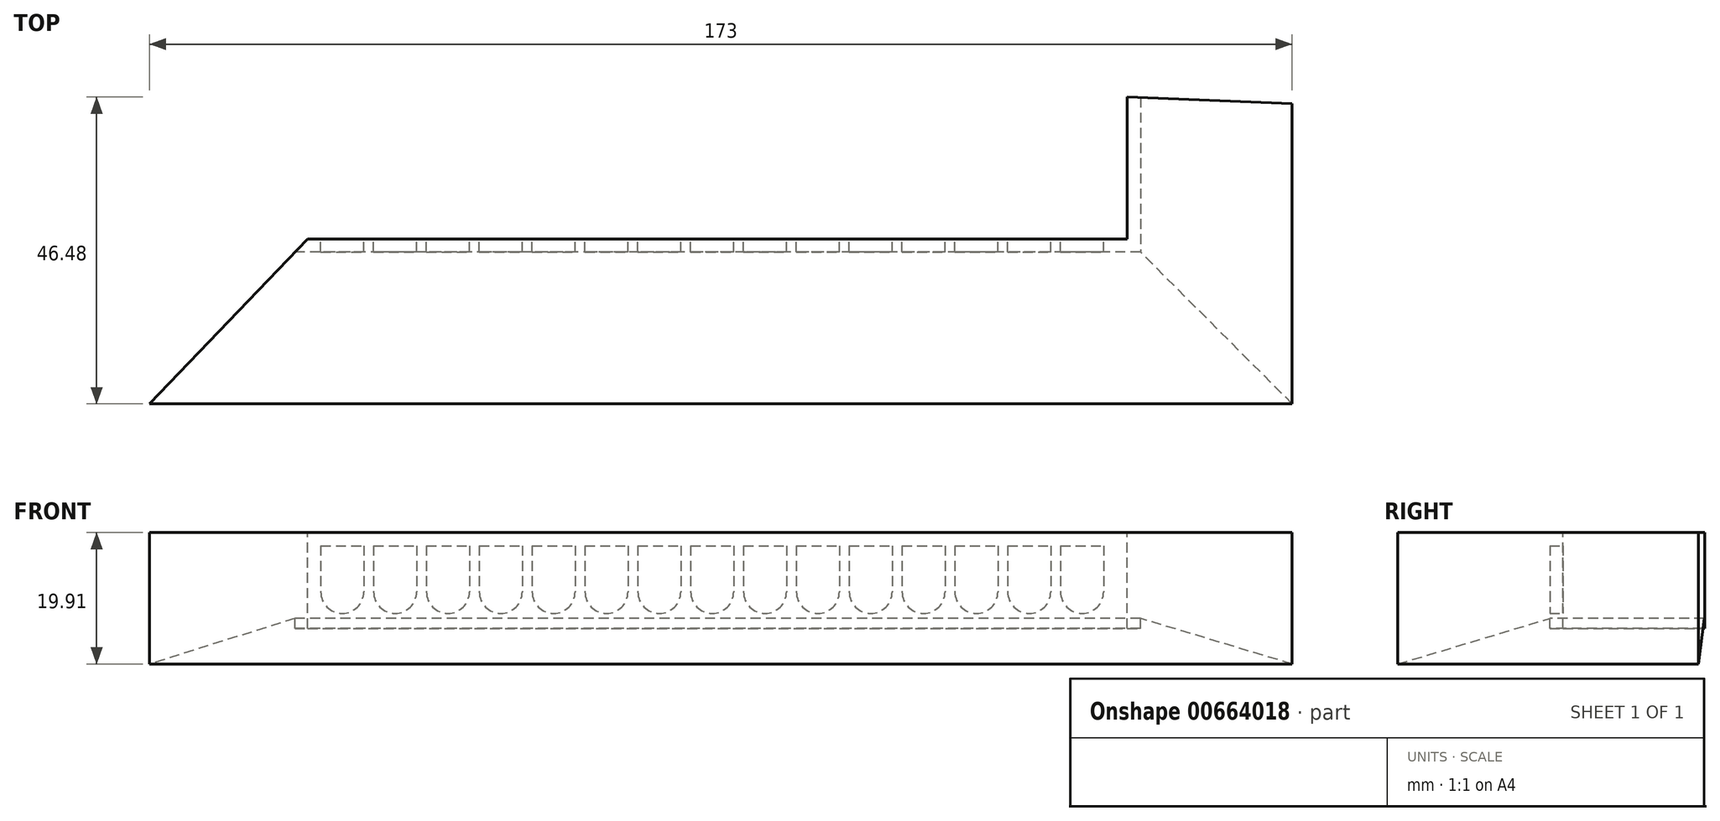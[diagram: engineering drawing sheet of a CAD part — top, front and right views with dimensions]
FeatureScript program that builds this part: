
annotation { "Feature Type Name" : "Feature", "Feature Type Description" : "" }
export const myFeature = defineFeature(function(context is Context, id is Id, definition is map)
    precondition{}
    {
        {
            var Q0;
            Q0=qCreatedBy(makeId("Top.planeOp"),FACE);
            var sketch = newSketch(context, id + "F0", { "sketchPlane" : qUnion([Q0])});
            skLineSegment(sketch, "E0", {"start": v(0, 0) * mm, "end": v(0, 45.5) * mm});
            skLineSegment(sketch, "E1", {"start": v(0, 45.5) * mm, "end": v(-22.98, 46.4) * mm});
            skLineSegment(sketch, "E2", {"start": v(-22.98, 46.4) * mm, "end": v(-22.98, 23) * mm});
            skLineSegment(sketch, "E3", {"start": v(-22.98, 23) * mm, "end": v(-150.98, 23) * mm});
            skLineSegment(sketch, "E4", {"start": v(-43.34, 0) * mm, "end": v(0, 0) * mm});
            skLineSegment(sketch, "E5", {"start": v(-150.98, 23) * mm, "end": v(-173, 0) * mm});
            skLineSegment(sketch, "E6", {"start": v(-173, 0) * mm, "end": v(-43.34, 0) * mm});
            skSolve(sketch);
        }
        {
            var Q0;
            Q0=makeQuery(id+"F0.imprint","IMPRINT",FACE,{"disambiguationData":[TD([[makeQuery(id+"F0.imprint","IMPRINT",EDGE,{"derivedFrom":sQuery(id+"F0.wireOp",EDGE,"E0")}),1.0]])]});
            extrude(context, id + "F1", {"entities" : qUnion([Q0]), "oppositeDirection" : true, "depth" : 13 * mm, "offsetDistance" : 25 * mm});
        }
        {
            var Q0;
            Q0=makeQuery(id+"F1.opExtrude","SWEPT_FACE",FACE,{"disambiguationData":[OSD([sQuery(id+"F0.wireOp",EDGE,"E4"),sQuery(id+"F0.wireOp",EDGE,"E6")])]});
            var sketch = newSketch(context, id + "F2", { "sketchPlane" : qUnion([Q0])});
            skLineSegment(sketch, "E7.0.0", {"start": v(-22.98, 0) * mm, "end": v(0, 0) * mm});
            skLineSegment(sketch, "E7.0.1", {"start": v(0, 0) * mm, "end": v(0, -13) * mm});
            skLineSegment(sketch, "E7.0.2", {"start": v(0, -13) * mm, "end": v(-22.98, -13) * mm});
            skLineSegment(sketch, "E7.0.3", {"start": v(-22.98, -13) * mm, "end": v(-22.98, 0) * mm});
            skLineSegment(sketch, "E8", {"start": v(-22.98, -13) * mm, "end": v(-20.98, -13) * mm});
            skLineSegment(sketch, "E9", {"start": v(-20.98, -13) * mm, "end": v(-22.98, -13) * mm});
            skLineSegment(sketch, "E10", {"start": v(-22.98, -13) * mm, "end": v(0, -19.91) * mm});
            skLineSegment(sketch, "E11", {"start": v(0, -19.91) * mm, "end": v(0, -13) * mm});
            skSolve(sketch);
        }
        {
            var Q0;
            {var subQ0=sQuery(id+"F2.wireOp",EDGE,"E10");Q0=makeQuery(id+"F2.imprint","IMPRINT",FACE,{"disambiguationData":[TD([[makeQuery(id+"F2.imprint","IMPRINT",EDGE,{"derivedFrom":subQ0}),1.0]])]});}
            var Q1;
            Q1=makeQuery(id+"F1.opExtrude","SWEPT_FACE",FACE,{"disambiguationData":[OSD([sQuery(id+"F0.wireOp",EDGE,"E1")])]});
            extrude(context, id + "F3", {"entities" : qUnion([Q0]), "operationType" : NewBodyOperationType.ADD, "endBound" : BoundingType.UP_TO_SURFACE, "oppositeDirection" : true, "depth" : 25 * mm, "endBoundEntityFace" : qUnion([Q1]), "offsetDistance" : 25 * mm});
        }
        {
            var Q0;
            Q0=makeQuery(id+"F3.boolean.opBoolean","MERGE",FACE,{"derivedFrom":[makeQuery(id+"F1.opExtrude","SWEPT_FACE",FACE,{"disambiguationData":[OSD([sQuery(id+"F0.wireOp",EDGE,"E0")])]}),makeQuery(id+"F3.opExtrude","SWEPT_FACE",FACE,{"disambiguationData":[OSD([sQuery(id+"F2.wireOp",EDGE,"E11")])]})]});
            var sketch = newSketch(context, id + "F4", { "sketchPlane" : qUnion([Q0])});
            skLineSegment(sketch, "E12.0.0", {"start": v(0, 0) * mm, "end": v(23, 0) * mm});
            skLineSegment(sketch, "E12.0.1", {"start": v(23, 0) * mm, "end": v(23, -13) * mm});
            skLineSegment(sketch, "E12.0.2", {"start": v(23, -13) * mm, "end": v(0, -13) * mm});
            skLineSegment(sketch, "E12.0.3", {"start": v(0, -13) * mm, "end": v(0, 0) * mm});
            skLineSegment(sketch, "E13", {"start": v(23, -13) * mm, "end": v(0, -19.91) * mm});
            skLineSegment(sketch, "E14", {"start": v(0, -19.91) * mm, "end": v(0, -13) * mm});
            skSolve(sketch);
        }
        {
            var Q0;
            Q0=makeQuery(id+"F4.imprint","IMPRINT",FACE,{"disambiguationData":[TD([[makeQuery(id+"F4.imprint","IMPRINT",EDGE,{"derivedFrom":sQuery(id+"F4.wireOp",EDGE,"E12.0.2")}),1.0]])]});
            var Q1;
            Q1=makeQuery(id+"F1.opExtrude","SWEPT_FACE",FACE,{"disambiguationData":[OSD([sQuery(id+"F0.wireOp",EDGE,"E5")])]});
            extrude(context, id + "F5", {"entities" : qUnion([Q0]), "operationType" : NewBodyOperationType.ADD, "endBound" : BoundingType.UP_TO_SURFACE, "oppositeDirection" : true, "depth" : 25 * mm, "endBoundEntityFace" : qUnion([Q1]), "offsetDistance" : 25 * mm});
        }
        {
            var Q0;
            Q0=makeQuery(id+"F0.imprint","IMPRINT",FACE,{"disambiguationData":[TD([[makeQuery(id+"F0.imprint","IMPRINT",EDGE,{"derivedFrom":sQuery(id+"F0.wireOp",EDGE,"E0")}),1.0]])]});
            var sketch = newSketch(context, id + "F6", { "sketchPlane" : qUnion([Q0])});
            skLineSegment(sketch, "E15.0.0", {"start": v(-150.98, 23) * mm, "end": v(-173, 0) * mm});
            skLineSegment(sketch, "E15.0.1", {"start": v(-173, 0) * mm, "end": v(-43.34, 0) * mm});
            skLineSegment(sketch, "E15.0.2", {"start": v(-43.34, 0) * mm, "end": v(0, 0) * mm});
            skLineSegment(sketch, "E15.0.3", {"start": v(0, 0) * mm, "end": v(0, 45.5) * mm});
            skLineSegment(sketch, "E15.0.4", {"start": v(0, 45.5) * mm, "end": v(-22.98, 46.4) * mm});
            skLineSegment(sketch, "E15.0.5", {"start": v(-22.98, 46.4) * mm, "end": v(-22.98, 23) * mm});
            skLineSegment(sketch, "E15.0.6", {"start": v(-22.98, 23) * mm, "end": v(-150.98, 23) * mm});
            skLineSegment(sketch, "E16", {"start": v(-150.98, 23) * mm, "end": v(-149.07, 25) * mm});
            skLineSegment(sketch, "E17", {"start": v(-149.07, 25) * mm, "end": v(-24.98, 25) * mm});
            skLineSegment(sketch, "E18", {"start": v(-24.98, 25) * mm, "end": v(-24.98, 46.48) * mm});
            skLineSegment(sketch, "E19", {"start": v(-24.98, 46.48) * mm, "end": v(-22.98, 46.4) * mm});
            skSolve(sketch);
        }
        {
            var Q0;
            Q0=makeQuery(id+"F6.imprint","IMPRINT",FACE,{"disambiguationData":[TD([[makeQuery(id+"F6.imprint","IMPRINT",EDGE,{"derivedFrom":sQuery(id+"F6.wireOp",EDGE,"E15.0.5")}),-1.0]])]});
            extrude(context, id + "F7", {"entities" : qUnion([Q0]), "operationType" : NewBodyOperationType.ADD, "oppositeDirection" : true, "depth" : 14.5 * mm, "offsetDistance" : 25 * mm});
        }
        {
            var Q0;
            Q0=makeQuery(id+"F7.opExtrude","SWEPT_FACE",FACE,{"disambiguationData":[OSD([sQuery(id+"F6.wireOp",EDGE,"E17")])]});
            var sketch = newSketch(context, id + "F8", { "sketchPlane" : qUnion([Q0])});
            skLineSegment(sketch, "E20.bottom", {"start": v(147.07, -2) * mm, "end": v(140.57, -2) * mm});
            skLineSegment(sketch, "E20.top", {"start": v(147.07, -9) * mm, "end": v(140.57, -9) * mm});
            skLineSegment(sketch, "E20.left", {"start": v(147.07, -2) * mm, "end": v(147.07, -9) * mm});
            skLineSegment(sketch, "E20.right", {"start": v(140.57, -2) * mm, "end": v(140.57, -9) * mm});
            skArc(sketch, "E21", {"start": v(140.57, -9) * mm, "mid": v(143.82, -12.25) * mm, "end": v(147.07, -9) * mm});
            skLineSegment(sketch, "E22.1.0.0", {"start": v(132.57, -2) * mm, "end": v(132.57, -9) * mm});
            skLineSegment(sketch, "E22.1.0.1", {"start": v(139.07, -2) * mm, "end": v(139.07, -9) * mm});
            skLineSegment(sketch, "E22.1.0.2", {"start": v(139.07, -2) * mm, "end": v(132.57, -2) * mm});
            skLineSegment(sketch, "E22.1.0.3", {"start": v(139.07, -9) * mm, "end": v(132.57, -9) * mm});
            skArc(sketch, "E22.1.0.4", {"start": v(132.57, -9) * mm, "mid": v(135.82, -12.25) * mm, "end": v(139.07, -9) * mm});
            skLineSegment(sketch, "E22.2.0.0", {"start": v(124.57, -2) * mm, "end": v(124.57, -9) * mm});
            skLineSegment(sketch, "E22.2.0.1", {"start": v(131.07, -2) * mm, "end": v(131.07, -9) * mm});
            skLineSegment(sketch, "E22.2.0.2", {"start": v(131.07, -2) * mm, "end": v(124.57, -2) * mm});
            skLineSegment(sketch, "E22.2.0.3", {"start": v(131.07, -9) * mm, "end": v(124.57, -9) * mm});
            skArc(sketch, "E22.2.0.4", {"start": v(124.57, -9) * mm, "mid": v(127.82, -12.25) * mm, "end": v(131.07, -9) * mm});
            skLineSegment(sketch, "E22.3.0.0", {"start": v(116.57, -2) * mm, "end": v(116.57, -9) * mm});
            skLineSegment(sketch, "E22.3.0.1", {"start": v(123.07, -2) * mm, "end": v(123.07, -9) * mm});
            skLineSegment(sketch, "E22.3.0.2", {"start": v(123.07, -2) * mm, "end": v(116.57, -2) * mm});
            skLineSegment(sketch, "E22.3.0.3", {"start": v(123.07, -9) * mm, "end": v(116.57, -9) * mm});
            skArc(sketch, "E22.3.0.4", {"start": v(116.57, -9) * mm, "mid": v(119.82, -12.25) * mm, "end": v(123.07, -9) * mm});
            skLineSegment(sketch, "E22.4.0.0", {"start": v(108.57, -2) * mm, "end": v(108.57, -9) * mm});
            skLineSegment(sketch, "E22.4.0.1", {"start": v(115.07, -2) * mm, "end": v(115.07, -9) * mm});
            skLineSegment(sketch, "E22.4.0.2", {"start": v(115.07, -2) * mm, "end": v(108.57, -2) * mm});
            skLineSegment(sketch, "E22.4.0.3", {"start": v(115.07, -9) * mm, "end": v(108.57, -9) * mm});
            skArc(sketch, "E22.4.0.4", {"start": v(108.57, -9) * mm, "mid": v(111.82, -12.25) * mm, "end": v(115.07, -9) * mm});
            skLineSegment(sketch, "E22.5.0.0", {"start": v(100.57, -2) * mm, "end": v(100.57, -9) * mm});
            skLineSegment(sketch, "E22.5.0.1", {"start": v(107.07, -2) * mm, "end": v(107.07, -9) * mm});
            skLineSegment(sketch, "E22.5.0.2", {"start": v(107.07, -2) * mm, "end": v(100.57, -2) * mm});
            skLineSegment(sketch, "E22.5.0.3", {"start": v(107.07, -9) * mm, "end": v(100.57, -9) * mm});
            skArc(sketch, "E22.5.0.4", {"start": v(100.57, -9) * mm, "mid": v(103.82, -12.25) * mm, "end": v(107.07, -9) * mm});
            skLineSegment(sketch, "E22.6.0.0", {"start": v(92.57, -2) * mm, "end": v(92.57, -9) * mm});
            skLineSegment(sketch, "E22.6.0.1", {"start": v(99.07, -2) * mm, "end": v(99.07, -9) * mm});
            skLineSegment(sketch, "E22.6.0.2", {"start": v(99.07, -2) * mm, "end": v(92.57, -2) * mm});
            skLineSegment(sketch, "E22.6.0.3", {"start": v(99.07, -9) * mm, "end": v(92.57, -9) * mm});
            skArc(sketch, "E22.6.0.4", {"start": v(92.57, -9) * mm, "mid": v(95.82, -12.25) * mm, "end": v(99.07, -9) * mm});
            skLineSegment(sketch, "E22.7.0.0", {"start": v(84.57, -2) * mm, "end": v(84.57, -9) * mm});
            skLineSegment(sketch, "E22.7.0.1", {"start": v(91.07, -2) * mm, "end": v(91.07, -9) * mm});
            skLineSegment(sketch, "E22.7.0.2", {"start": v(91.07, -2) * mm, "end": v(84.57, -2) * mm});
            skLineSegment(sketch, "E22.7.0.3", {"start": v(91.07, -9) * mm, "end": v(84.57, -9) * mm});
            skArc(sketch, "E22.7.0.4", {"start": v(84.57, -9) * mm, "mid": v(87.82, -12.25) * mm, "end": v(91.07, -9) * mm});
            skLineSegment(sketch, "E22.8.0.0", {"start": v(76.57, -2) * mm, "end": v(76.57, -9) * mm});
            skLineSegment(sketch, "E22.8.0.1", {"start": v(83.07, -2) * mm, "end": v(83.07, -9) * mm});
            skLineSegment(sketch, "E22.8.0.2", {"start": v(83.07, -2) * mm, "end": v(76.57, -2) * mm});
            skLineSegment(sketch, "E22.8.0.3", {"start": v(83.07, -9) * mm, "end": v(76.57, -9) * mm});
            skArc(sketch, "E22.8.0.4", {"start": v(76.57, -9) * mm, "mid": v(79.82, -12.25) * mm, "end": v(83.07, -9) * mm});
            skLineSegment(sketch, "E22.9.0.0", {"start": v(68.57, -2) * mm, "end": v(68.57, -9) * mm});
            skLineSegment(sketch, "E22.9.0.1", {"start": v(75.07, -2) * mm, "end": v(75.07, -9) * mm});
            skLineSegment(sketch, "E22.9.0.2", {"start": v(75.07, -2) * mm, "end": v(68.57, -2) * mm});
            skLineSegment(sketch, "E22.9.0.3", {"start": v(75.07, -9) * mm, "end": v(68.57, -9) * mm});
            skArc(sketch, "E22.9.0.4", {"start": v(68.57, -9) * mm, "mid": v(71.82, -12.25) * mm, "end": v(75.07, -9) * mm});
            skLineSegment(sketch, "E22.10.0.0", {"start": v(60.57, -2) * mm, "end": v(60.57, -9) * mm});
            skLineSegment(sketch, "E22.10.0.1", {"start": v(67.07, -2) * mm, "end": v(67.07, -9) * mm});
            skLineSegment(sketch, "E22.10.0.2", {"start": v(67.07, -2) * mm, "end": v(60.57, -2) * mm});
            skLineSegment(sketch, "E22.10.0.3", {"start": v(67.07, -9) * mm, "end": v(60.57, -9) * mm});
            skArc(sketch, "E22.10.0.4", {"start": v(60.57, -9) * mm, "mid": v(63.82, -12.25) * mm, "end": v(67.07, -9) * mm});
            skLineSegment(sketch, "E22.11.0.0", {"start": v(52.57, -2) * mm, "end": v(52.57, -9) * mm});
            skLineSegment(sketch, "E22.11.0.1", {"start": v(59.07, -2) * mm, "end": v(59.07, -9) * mm});
            skLineSegment(sketch, "E22.11.0.2", {"start": v(59.07, -2) * mm, "end": v(52.57, -2) * mm});
            skLineSegment(sketch, "E22.11.0.3", {"start": v(59.07, -9) * mm, "end": v(52.57, -9) * mm});
            skArc(sketch, "E22.11.0.4", {"start": v(52.57, -9) * mm, "mid": v(55.82, -12.25) * mm, "end": v(59.07, -9) * mm});
            skLineSegment(sketch, "E22.12.0.0", {"start": v(44.57, -2) * mm, "end": v(44.57, -9) * mm});
            skLineSegment(sketch, "E22.12.0.1", {"start": v(51.07, -2) * mm, "end": v(51.07, -9) * mm});
            skLineSegment(sketch, "E22.12.0.2", {"start": v(51.07, -2) * mm, "end": v(44.57, -2) * mm});
            skLineSegment(sketch, "E22.12.0.3", {"start": v(51.07, -9) * mm, "end": v(44.57, -9) * mm});
            skArc(sketch, "E22.12.0.4", {"start": v(44.57, -9) * mm, "mid": v(47.82, -12.25) * mm, "end": v(51.07, -9) * mm});
            skLineSegment(sketch, "E22.13.0.0", {"start": v(36.57, -2) * mm, "end": v(36.57, -9) * mm});
            skLineSegment(sketch, "E22.13.0.1", {"start": v(43.07, -2) * mm, "end": v(43.07, -9) * mm});
            skLineSegment(sketch, "E22.13.0.2", {"start": v(43.07, -2) * mm, "end": v(36.57, -2) * mm});
            skLineSegment(sketch, "E22.13.0.3", {"start": v(43.07, -9) * mm, "end": v(36.57, -9) * mm});
            skArc(sketch, "E22.13.0.4", {"start": v(36.57, -9) * mm, "mid": v(39.82, -12.25) * mm, "end": v(43.07, -9) * mm});
            skLineSegment(sketch, "E22.direction1", {"start": v(140.57, -9) * mm, "end": v(132.57, -9) * mm, "construction": true});
            skLineSegment(sketch, "E23.0.14.0", {"start": v(28.57, -2) * mm, "end": v(28.57, -9) * mm});
            skLineSegment(sketch, "E23.3.14.0", {"start": v(35.07, -2) * mm, "end": v(35.07, -9) * mm});
            skLineSegment(sketch, "E23.6.14.0", {"start": v(35.07, -2) * mm, "end": v(28.57, -2) * mm});
            skLineSegment(sketch, "E23.9.14.0", {"start": v(35.07, -9) * mm, "end": v(28.57, -9) * mm});
            skArc(sketch, "E23.12.14.0", {"start": v(28.57, -9) * mm, "mid": v(31.82, -12.25) * mm, "end": v(35.07, -9) * mm});
            skSolve(sketch);
        }
        {
            var Q0;
            Q0=makeQuery(id+"F8.imprint","IMPRINT",FACE,{"disambiguationData":[TD([[makeQuery(id+"F8.imprint","IMPRINT",EDGE,{"derivedFrom":sQuery(id+"F8.wireOp",EDGE,"E20.bottom")}),1.0]])]});
            var Q1;
            Q1=makeQuery(id+"F8.imprint","IMPRINT",FACE,{"disambiguationData":[TD([[makeQuery(id+"F8.imprint","IMPRINT",EDGE,{"derivedFrom":sQuery(id+"F8.wireOp",EDGE,"E20.top")}),1.0]])]});
            var Q2;
            Q2=makeQuery(id+"F8.imprint","IMPRINT",FACE,{"disambiguationData":[TD([[makeQuery(id+"F8.imprint","IMPRINT",EDGE,{"derivedFrom":sQuery(id+"F8.wireOp",EDGE,"E22.1.0.3")}),1.0]])]});
            var Q3;
            Q3=makeQuery(id+"F8.imprint","IMPRINT",FACE,{"disambiguationData":[TD([[makeQuery(id+"F8.imprint","IMPRINT",EDGE,{"derivedFrom":sQuery(id+"F8.wireOp",EDGE,"E22.1.0.0")}),1.0]])]});
            var Q4;
            Q4=makeQuery(id+"F8.imprint","IMPRINT",FACE,{"disambiguationData":[TD([[makeQuery(id+"F8.imprint","IMPRINT",EDGE,{"derivedFrom":sQuery(id+"F8.wireOp",EDGE,"E22.2.0.0")}),1.0]])]});
            var Q5;
            Q5=makeQuery(id+"F8.imprint","IMPRINT",FACE,{"disambiguationData":[TD([[makeQuery(id+"F8.imprint","IMPRINT",EDGE,{"derivedFrom":sQuery(id+"F8.wireOp",EDGE,"E22.3.0.0")}),1.0]])]});
            var Q6;
            Q6=makeQuery(id+"F8.imprint","IMPRINT",FACE,{"disambiguationData":[TD([[makeQuery(id+"F8.imprint","IMPRINT",EDGE,{"derivedFrom":sQuery(id+"F8.wireOp",EDGE,"E22.4.0.0")}),1.0]])]});
            var Q7;
            Q7=makeQuery(id+"F8.imprint","IMPRINT",FACE,{"disambiguationData":[TD([[makeQuery(id+"F8.imprint","IMPRINT",EDGE,{"derivedFrom":sQuery(id+"F8.wireOp",EDGE,"E22.5.0.0")}),1.0]])]});
            var Q8;
            Q8=makeQuery(id+"F8.imprint","IMPRINT",FACE,{"disambiguationData":[TD([[makeQuery(id+"F8.imprint","IMPRINT",EDGE,{"derivedFrom":sQuery(id+"F8.wireOp",EDGE,"E22.6.0.0")}),1.0]])]});
            var Q9;
            Q9=makeQuery(id+"F8.imprint","IMPRINT",FACE,{"disambiguationData":[TD([[makeQuery(id+"F8.imprint","IMPRINT",EDGE,{"derivedFrom":sQuery(id+"F8.wireOp",EDGE,"E22.7.0.0")}),1.0]])]});
            var Q10;
            Q10=makeQuery(id+"F8.imprint","IMPRINT",FACE,{"disambiguationData":[TD([[makeQuery(id+"F8.imprint","IMPRINT",EDGE,{"derivedFrom":sQuery(id+"F8.wireOp",EDGE,"E22.8.0.0")}),1.0]])]});
            var Q11;
            Q11=makeQuery(id+"F8.imprint","IMPRINT",FACE,{"disambiguationData":[TD([[makeQuery(id+"F8.imprint","IMPRINT",EDGE,{"derivedFrom":sQuery(id+"F8.wireOp",EDGE,"E22.9.0.0")}),1.0]])]});
            var Q12;
            Q12=makeQuery(id+"F8.imprint","IMPRINT",FACE,{"disambiguationData":[TD([[makeQuery(id+"F8.imprint","IMPRINT",EDGE,{"derivedFrom":sQuery(id+"F8.wireOp",EDGE,"E22.10.0.0")}),1.0]])]});
            var Q13;
            Q13=makeQuery(id+"F8.imprint","IMPRINT",FACE,{"disambiguationData":[TD([[makeQuery(id+"F8.imprint","IMPRINT",EDGE,{"derivedFrom":sQuery(id+"F8.wireOp",EDGE,"E22.11.0.0")}),1.0]])]});
            var Q14;
            Q14=makeQuery(id+"F8.imprint","IMPRINT",FACE,{"disambiguationData":[TD([[makeQuery(id+"F8.imprint","IMPRINT",EDGE,{"derivedFrom":sQuery(id+"F8.wireOp",EDGE,"E22.12.0.0")}),1.0]])]});
            var Q15;
            Q15=makeQuery(id+"F8.imprint","IMPRINT",FACE,{"disambiguationData":[TD([[makeQuery(id+"F8.imprint","IMPRINT",EDGE,{"derivedFrom":sQuery(id+"F8.wireOp",EDGE,"E22.13.0.0")}),1.0]])]});
            var Q16;
            Q16=makeQuery(id+"F8.imprint","IMPRINT",FACE,{"disambiguationData":[TD([[makeQuery(id+"F8.imprint","IMPRINT",EDGE,{"derivedFrom":sQuery(id+"F8.wireOp",EDGE,"E23.0.14.0")}),1.0]])]});
            var Q17;
            Q17=makeQuery(id+"F8.imprint","IMPRINT",FACE,{"disambiguationData":[TD([[makeQuery(id+"F8.imprint","IMPRINT",EDGE,{"derivedFrom":sQuery(id+"F8.wireOp",EDGE,"E23.9.14.0")}),1.0]])]});
            var Q18;
            Q18=makeQuery(id+"F8.imprint","IMPRINT",FACE,{"disambiguationData":[TD([[makeQuery(id+"F8.imprint","IMPRINT",EDGE,{"derivedFrom":sQuery(id+"F8.wireOp",EDGE,"E22.13.0.3")}),1.0]])]});
            var Q19;
            Q19=makeQuery(id+"F8.imprint","IMPRINT",FACE,{"disambiguationData":[TD([[makeQuery(id+"F8.imprint","IMPRINT",EDGE,{"derivedFrom":sQuery(id+"F8.wireOp",EDGE,"E22.12.0.3")}),1.0]])]});
            var Q20;
            Q20=makeQuery(id+"F8.imprint","IMPRINT",FACE,{"disambiguationData":[TD([[makeQuery(id+"F8.imprint","IMPRINT",EDGE,{"derivedFrom":sQuery(id+"F8.wireOp",EDGE,"E22.11.0.3")}),1.0]])]});
            var Q21;
            Q21=makeQuery(id+"F8.imprint","IMPRINT",FACE,{"disambiguationData":[TD([[makeQuery(id+"F8.imprint","IMPRINT",EDGE,{"derivedFrom":sQuery(id+"F8.wireOp",EDGE,"E22.10.0.3")}),1.0]])]});
            var Q22;
            Q22=makeQuery(id+"F8.imprint","IMPRINT",FACE,{"disambiguationData":[TD([[makeQuery(id+"F8.imprint","IMPRINT",EDGE,{"derivedFrom":sQuery(id+"F8.wireOp",EDGE,"E22.9.0.3")}),1.0]])]});
            var Q23;
            Q23=makeQuery(id+"F8.imprint","IMPRINT",FACE,{"disambiguationData":[TD([[makeQuery(id+"F8.imprint","IMPRINT",EDGE,{"derivedFrom":sQuery(id+"F8.wireOp",EDGE,"E22.8.0.3")}),1.0]])]});
            var Q24;
            Q24=makeQuery(id+"F8.imprint","IMPRINT",FACE,{"disambiguationData":[TD([[makeQuery(id+"F8.imprint","IMPRINT",EDGE,{"derivedFrom":sQuery(id+"F8.wireOp",EDGE,"E22.7.0.3")}),1.0]])]});
            var Q25;
            Q25=makeQuery(id+"F8.imprint","IMPRINT",FACE,{"disambiguationData":[TD([[makeQuery(id+"F8.imprint","IMPRINT",EDGE,{"derivedFrom":sQuery(id+"F8.wireOp",EDGE,"E22.6.0.3")}),1.0]])]});
            var Q26;
            Q26=makeQuery(id+"F8.imprint","IMPRINT",FACE,{"disambiguationData":[TD([[makeQuery(id+"F8.imprint","IMPRINT",EDGE,{"derivedFrom":sQuery(id+"F8.wireOp",EDGE,"E22.5.0.3")}),1.0]])]});
            var Q27;
            Q27=makeQuery(id+"F8.imprint","IMPRINT",FACE,{"disambiguationData":[TD([[makeQuery(id+"F8.imprint","IMPRINT",EDGE,{"derivedFrom":sQuery(id+"F8.wireOp",EDGE,"E22.4.0.3")}),1.0]])]});
            var Q28;
            Q28=makeQuery(id+"F8.imprint","IMPRINT",FACE,{"disambiguationData":[TD([[makeQuery(id+"F8.imprint","IMPRINT",EDGE,{"derivedFrom":sQuery(id+"F8.wireOp",EDGE,"E22.3.0.3")}),1.0]])]});
            var Q29;
            Q29=makeQuery(id+"F8.imprint","IMPRINT",FACE,{"disambiguationData":[TD([[makeQuery(id+"F8.imprint","IMPRINT",EDGE,{"derivedFrom":sQuery(id+"F8.wireOp",EDGE,"E22.2.0.3")}),1.0]])]});
            extrude(context, id + "F9", {"entities" : qUnion([Q0, Q1, Q2, Q3, Q4, Q5, Q6, Q7, Q8, Q9, Q10, Q11, Q12, Q13, Q14, Q15, Q16, Q17, Q18, Q19, Q20, Q21, Q22, Q23, Q24, Q25, Q26, Q27, Q28, Q29]), "operationType" : NewBodyOperationType.REMOVE, "oppositeDirection" : true, "depth" : 2 * mm, "offsetDistance" : 25 * mm});
        }
    });
